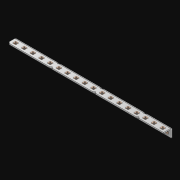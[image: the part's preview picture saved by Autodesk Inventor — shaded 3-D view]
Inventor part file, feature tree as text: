
AUTODESK INVENTOR PART (.ipt)
format: ipt  version: 2021 (Build 250183000, 183)  size: 698,368 bytes
history: native  units: in
note: dims shown in document units (in); Inventor stores cm internally (conversion verified against a paired STEP export)
features: extrude x37, other x36, sketch x3, pattern_linear x1, sheet_metal_op x1
ambient origin geometry x8: Origin, YZ Plane, XZ Plane, XY Plane, X Axis, Y Axis, Z Axis, Center Point
bodies: Solid1 (feature_tree)
feature tree (78):
  pattern_linear  "Rectangular Pattern1"  Spacing1=0.063in  [1 undecoded]
  extrude  "Extrusion1"  Depth=0.5in
  sketch  "Sketch1"  dims[d0=0.182in]
  other  "Srf1"
  sketch  "Sketch2"  dims[d1=0.063in d2=0.0in]
  other  "Srf2"
  other  "Srf3"
  other  "Srf5"
  other  "Srf7"
  other  "Srf9"
  other  "Srf11"
  other  "Srf13"
  other  "Srf15"
  other  "Srf17"
  other  "Srf19"
  other  "Srf21"
  other  "Srf23"
  other  "Srf25"
  other  "Srf27"
  other  "Srf29"
  other  "Srf31"
  other  "Srf33"
  other  "Srf35"
  other  "Srf4"
  other  "Srf6"
  other  "Srf8"
  other  "Srf10"
  other  "Srf12"
  other  "Srf14"
  other  "Srf16"
  other  "Srf18"
  other  "Srf20"
  other  "Srf22"
  other  "Srf24"
  other  "Srf26"
  other  "Srf28"
  other  "Srf30"
  other  "Srf32"
  other  "Srf34"
  other  "Srf36"
  sketch  "Sketch3"  dims[d3=0.182in d4=0.063in d5=0.0in d8=0.5in d9=8.5in d10=0.0in]
  sheet_metal_op  "Fold1"
  extrude  "ExtrusionSrf1"  Depth=8.5in TaperAngle=0.0deg
  extrude  "ExtrusionSrf2"  [1 undecoded]
  extrude  "ExtrusionSrf3"  [1 undecoded]
  extrude  "ExtrusionSrf4"  [1 undecoded]
  extrude  "ExtrusionSrf5"  [1 undecoded]
  extrude  "ExtrusionSrf6"  [1 undecoded]
  extrude  "ExtrusionSrf7"  [1 undecoded]
  extrude  "ExtrusionSrf8"  [1 undecoded]
  extrude  "ExtrusionSrf9"  [1 undecoded]
  extrude  "ExtrusionSrf10"  [1 undecoded]
  extrude  "ExtrusionSrf11"  [1 undecoded]
  extrude  "ExtrusionSrf12"  [1 undecoded]
  extrude  "ExtrusionSrf13"  [1 undecoded]
  extrude  "ExtrusionSrf14"  [1 undecoded]
  extrude  "ExtrusionSrf15"  [1 undecoded]
  extrude  "ExtrusionSrf16"  [1 undecoded]
  extrude  "ExtrusionSrf17"  [1 undecoded]
  extrude  "ExtrusionSrf18"  [1 undecoded]
  extrude  "ExtrusionSrf19"  [1 undecoded]
  extrude  "ExtrusionSrf37"  [1 undecoded]
  extrude  "ExtrusionSrf38"  [1 undecoded]
  extrude  "ExtrusionSrf39"  [1 undecoded]
  extrude  "ExtrusionSrf40"  [1 undecoded]
  extrude  "ExtrusionSrf41"  [1 undecoded]
  extrude  "ExtrusionSrf42"  [1 undecoded]
  extrude  "ExtrusionSrf43"  [1 undecoded]
  extrude  "ExtrusionSrf44"  [1 undecoded]
  extrude  "ExtrusionSrf45"  [1 undecoded]
  extrude  "ExtrusionSrf46"  [1 undecoded]
  extrude  "ExtrusionSrf47"  [1 undecoded]
  extrude  "ExtrusionSrf48"  [1 undecoded]
  extrude  "ExtrusionSrf49"  [1 undecoded]
  extrude  "ExtrusionSrf50"  [1 undecoded]
  extrude  "ExtrusionSrf51"  [1 undecoded]
  extrude  "ExtrusionSrf52"  [1 undecoded]
  extrude  "ExtrusionSrf53"  [1 undecoded]
note: 36 required parameter values undecoded (feature->parameter linkage not recoverable at this tier; creation-order binding heuristic only, values carry confidence <= 0.55)
